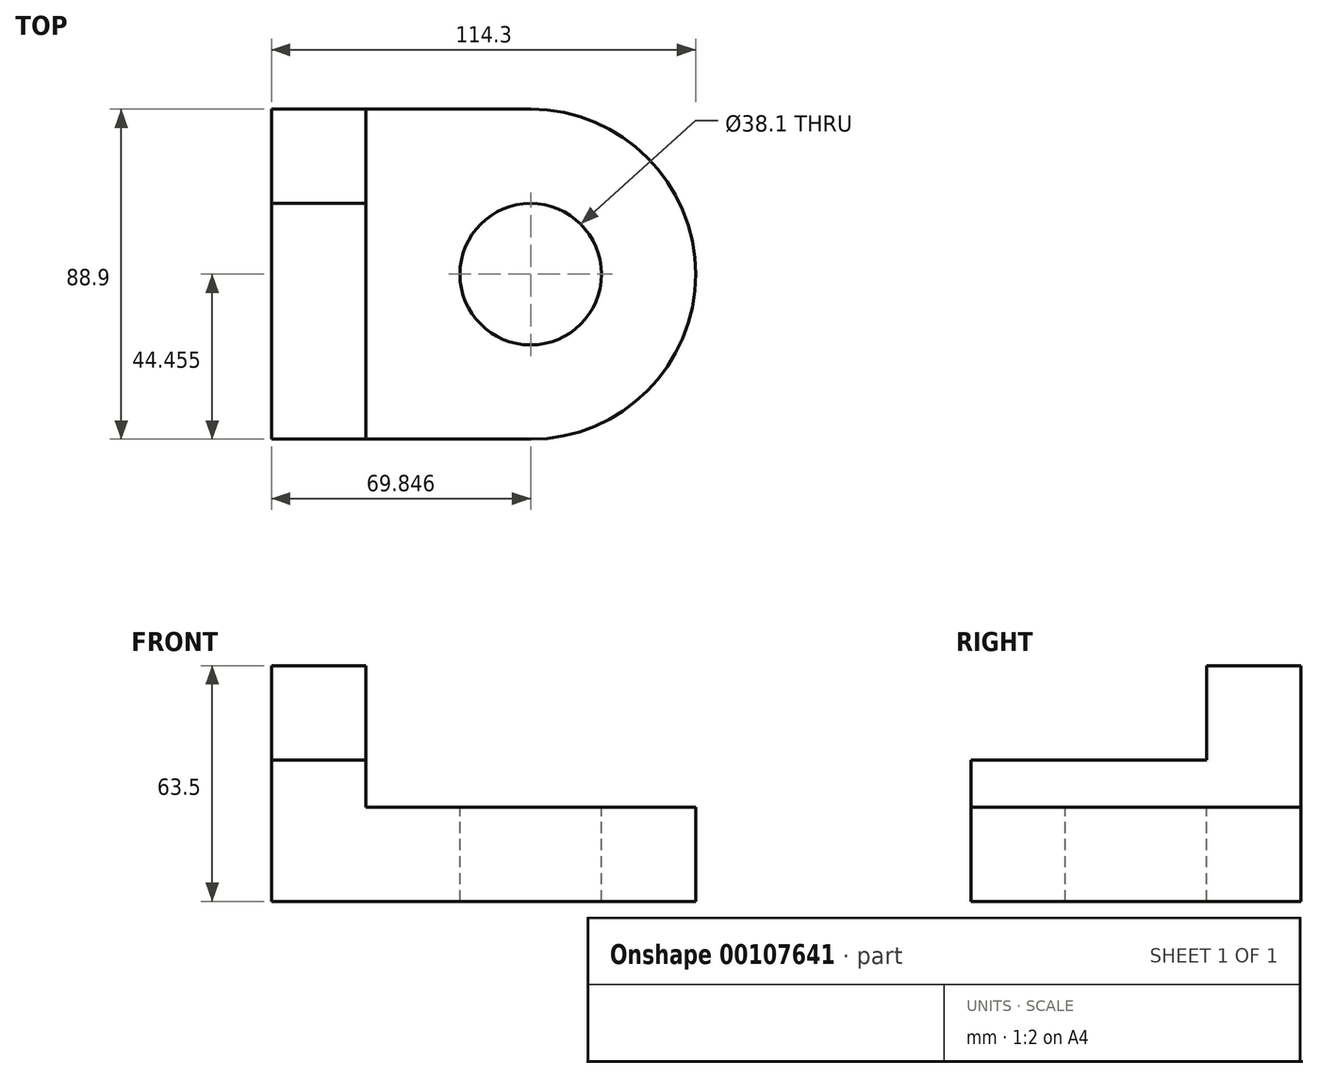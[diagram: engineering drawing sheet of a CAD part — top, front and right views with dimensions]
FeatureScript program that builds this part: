
annotation { "Feature Type Name" : "Feature", "Feature Type Description" : "" }
export const myFeature = defineFeature(function(context is Context, id is Id, definition is map)
    precondition{}
    {
        {
            var Q0;
            Q0=qCreatedBy(makeId("Top.planeOp"),FACE);
            var sketch = newSketch(context, id + "F0", { "sketchPlane" : qUnion([Q0])});
            skLineSegment(sketch, "E0", {"start": v(-111.88, 16.42) * mm, "end": v(-111.88, -72.48) * mm});
            skLineSegment(sketch, "E1", {"start": v(-111.88, -72.48) * mm, "end": v(-86.48, -72.48) * mm});
            skLineSegment(sketch, "E2", {"start": v(-86.48, -72.48) * mm, "end": v(-86.48, 16.42) * mm});
            skLineSegment(sketch, "E3", {"start": v(-86.48, 16.42) * mm, "end": v(-111.88, 16.42) * mm});
            skLineSegment(sketch, "E4", {"start": v(-86.48, 16.42) * mm, "end": v(-42.03, 16.42) * mm});
            skLineSegment(sketch, "E5", {"start": v(-86.48, -72.48) * mm, "end": v(-42.03, -72.48) * mm});
            skArc(sketch, "E6", {"start": v(-42.03, 16.42) * mm, "mid": v(2.42, -28.03) * mm, "end": v(-42.03, -72.48) * mm});
            skSolve(sketch);
        }
        {
            var Q0;
            Q0 = qSketchRegion(id + "F0", true);
            extrude(context, id + "F1", {"entities" : qUnion([Q0]), "depth" : 25.4 * mm});
        }
        {
            var Q0;
            Q0=makeQuery(id+"F1.opExtrude","CAP_FACE",FACE,{"disambiguationData":[OSD([sQuery(id+"F0.wireOp",EDGE,"E0"),sQuery(id+"F0.wireOp",EDGE,"E1"),sQuery(id+"F0.wireOp",EDGE,"E3"),sQuery(id+"F0.wireOp",EDGE,"E4"),sQuery(id+"F0.wireOp",EDGE,"E5"),sQuery(id+"F0.wireOp",EDGE,"E6")])],"isStart":false});
            var sketch = newSketch(context, id + "F2", { "sketchPlane" : qUnion([Q0])});
            skLineSegment(sketch, "E7", {"start": v(-86.48, 16.42) * mm, "end": v(-86.48, -8.98) * mm});
            skLineSegment(sketch, "E8", {"start": v(-86.48, -8.98) * mm, "end": v(-111.88, -8.98) * mm});
            skLineSegment(sketch, "E9", {"start": v(-111.88, -8.98) * mm, "end": v(-111.88, 16.42) * mm});
            skLineSegment(sketch, "E10", {"start": v(-111.88, 16.42) * mm, "end": v(-86.48, 16.42) * mm});
            skSolve(sketch);
        }
        {
            var Q0;
            Q0 = qSketchRegion(id + "F2", true);
            extrude(context, id + "F3", {"entities" : qUnion([Q0]), "operationType" : NewBodyOperationType.ADD, "depth" : 38.1 * mm});
        }
        {
            var Q0;
            Q0=makeQuery(id+"F1.opExtrude","CAP_FACE",FACE,{"disambiguationData":[OSD([sQuery(id+"F0.wireOp",EDGE,"E0"),sQuery(id+"F0.wireOp",EDGE,"E1"),sQuery(id+"F0.wireOp",EDGE,"E3"),sQuery(id+"F0.wireOp",EDGE,"E4"),sQuery(id+"F0.wireOp",EDGE,"E5"),sQuery(id+"F0.wireOp",EDGE,"E6")])],"isStart":false});
            var sketch = newSketch(context, id + "F4", { "sketchPlane" : qUnion([Q0])});
            skLineSegment(sketch, "E11", {"start": v(-111.88, -8.98) * mm, "end": v(-86.48, -8.98) * mm});
            skLineSegment(sketch, "E12", {"start": v(-86.48, -8.98) * mm, "end": v(-86.48, -72.48) * mm});
            skLineSegment(sketch, "E13", {"start": v(-86.48, -72.48) * mm, "end": v(-111.88, -72.48) * mm});
            skLineSegment(sketch, "E14", {"start": v(-111.88, -72.48) * mm, "end": v(-111.88, -8.98) * mm});
            skSolve(sketch);
        }
        {
            var Q0;
            Q0 = qSketchRegion(id + "F4", true);
            extrude(context, id + "F5", {"entities" : qUnion([Q0]), "operationType" : NewBodyOperationType.ADD, "depth" : 12.7 * mm});
        }
        {
            var Q0;
            Q0=makeQuery(id+"F1.opExtrude","CAP_FACE",FACE,{"disambiguationData":[OSD([sQuery(id+"F0.wireOp",EDGE,"E0"),sQuery(id+"F0.wireOp",EDGE,"E1"),sQuery(id+"F0.wireOp",EDGE,"E3"),sQuery(id+"F0.wireOp",EDGE,"E4"),sQuery(id+"F0.wireOp",EDGE,"E5"),sQuery(id+"F0.wireOp",EDGE,"E6")])],"isStart":false});
            var sketch = newSketch(context, id + "F6", { "sketchPlane" : qUnion([Q0])});
            skCircle(sketch, "E15", {"center": v(-42.03, -28.03) * mm, "radius": 19.05 * mm});
            skSolve(sketch);
        }
        {
            var Q0;
            Q0 = qSketchRegion(id + "F6", true);
            extrude(context, id + "F7", {"entities" : qUnion([Q0]), "operationType" : NewBodyOperationType.REMOVE, "oppositeDirection" : true, "depth" : 25.4 * mm});
        }
    });
